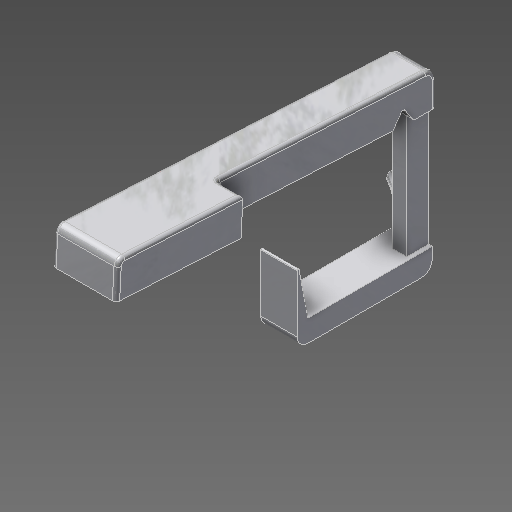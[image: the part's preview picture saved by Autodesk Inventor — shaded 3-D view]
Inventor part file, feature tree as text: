
AUTODESK INVENTOR PART (.ipt)
format: ipt  version: 2020 (Build 240168000, 168)  size: 334,848 bytes
history: native  units: mm
features: extrude x7, fillet x6, other x3, draft x1, chamfer x1
ambient origin geometry x8: Origin, YZ Plane, XZ Plane, XY Plane, X Axis, Y Axis, Z Axis, Center Point
bodies: Solid1 (feature_tree)
feature tree (18):
  other  "Key Sketch"
  extrude  "Upper Key"  Depth=10.0mm
  extrude  "Lower Key"  Depth=1.0mm
  other  "Hinge Cut Sketch"
  extrude  "Hinge Cut"  Depth=10.0mm TaperAngle=0.0deg
  extrude  "Hinge Cut 2"  Depth=3.0mm
  other  "Lever Sketch"
  extrude  "Vertical Lever"  Depth=3.0mm
  extrude  "Horizontal Lever"  Depth=33.6625mm
  extrude  "Spring Hook"  Depth=0.5mm
  draft  "FaceDraft3"
  chamfer  "Chamfer1"  Distance=3.0mm
  fillet  "Fillet9"  Radius=6.0mm
  fillet  "Fillet10"  Radius=4.0mm
  fillet  "Fillet5"  Radius=10.0mm
  fillet  "Fillet4"  [1 undecoded]
  fillet  "Fillet11"  Radius=3.0mm
  fillet  "Fillet14"  Radius=2.3mm
note: 1 required parameter value undecoded (feature->parameter linkage not recoverable at this tier; creation-order binding heuristic only, values carry confidence <= 0.55)
